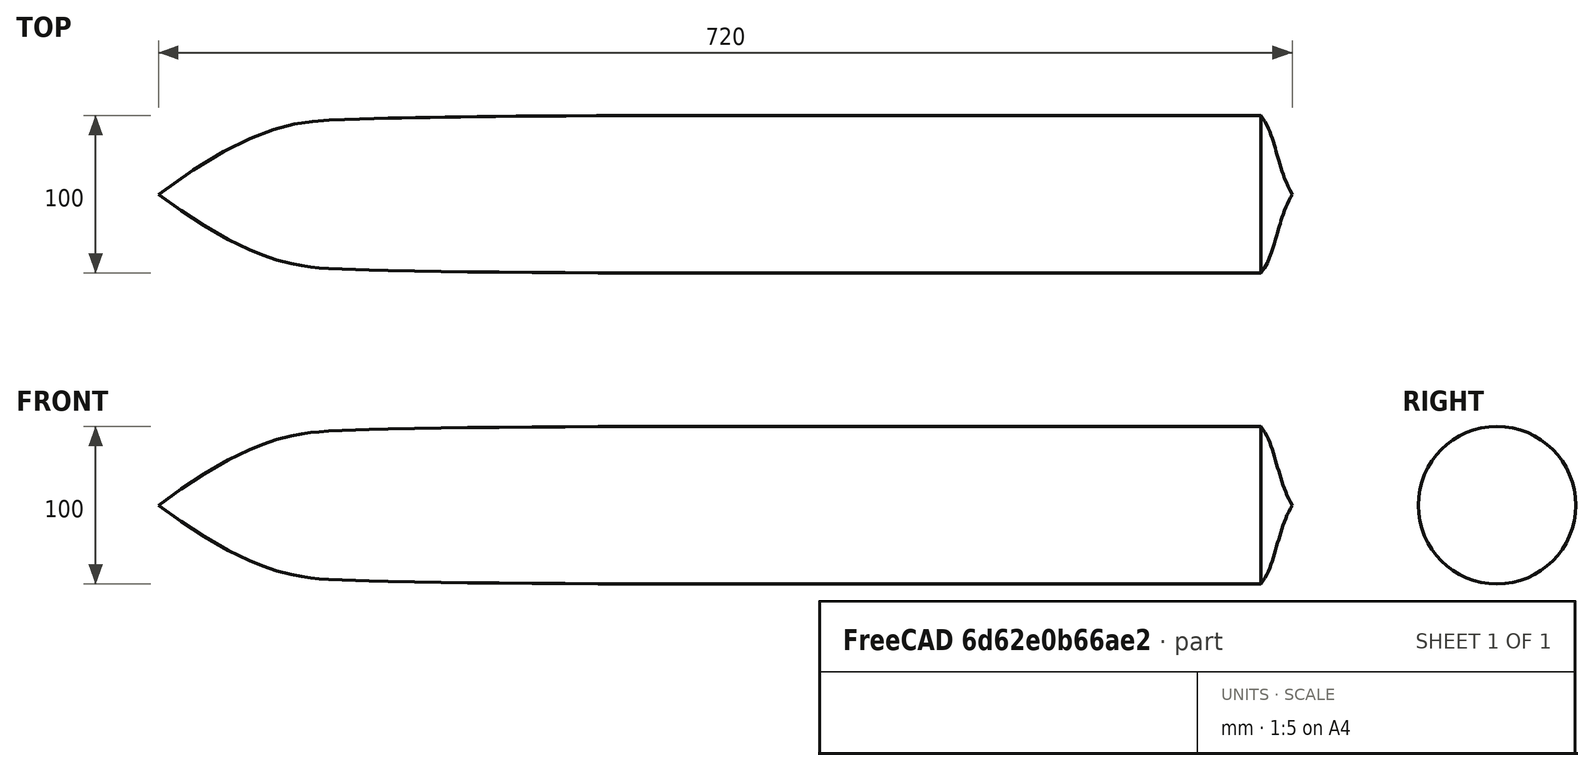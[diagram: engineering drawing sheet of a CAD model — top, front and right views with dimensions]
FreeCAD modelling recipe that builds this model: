
FCSTD DOCUMENT  (FreeCAD 0.19R24267 +99 (Git))
Label: Myring_hull_spreadsheet
License: All rights reserved
LicenseURL: http://en.wikipedia.org/wiki/All_rights_reserved
objects: Sketcher::SketchObject×1, PartDesign::Revolution×1, PartDesign::Body×1, TechDraw::DrawSVGTemplate×1, TechDraw::DrawViewPart×1, TechDraw::DrawViewSection×1, TechDraw::DrawPage×1, Spreadsheet::Sheet×1
note: 4 computed .brp shape members not serialized (recipe doc carries the construction recipe); baked Part::Feature solids carry a one-line shape summary decoded from their .brp

FEATURE [Sketcher::SketchObject] Sketch
  FullyConstrained = true
  MapMode = 5
  Support = -> [XY_Plane]
  expr: .Constraints.tail4_y = <<Parameters>>.tail4_y
  expr: .Constraints.tail2_y = <<Parameters>>.tail2_y
  expr: .Constraints.tail1_y = <<Parameters>>.tail1_y
  expr: .Constraints.nose4_y = <<Parameters>>.nose4_y
  expr: .Constraints.tail3_y = <<Parameters>>.tail3_y
  expr: .Constraints.nose3_y = <<Parameters>>.nose3_y
  expr: .Constraints.nose2_y = <<Parameters>>.nose2_y
  expr: .Constraints.myring_r = <<Parameters>>.myring_r
  expr: .Constraints.tail3_x = .Constraints.myring_c * 0.6
  expr: .Constraints.tail1_x = .Constraints.myring_c * 0.2
  expr: .Constraints.tail4_x = .Constraints.myring_c * 0.8
  expr: .Constraints.nose4_x = .Constraints.myring_a * 4 / 5
  expr: .Constraints.tail2_x = .Constraints.myring_c * 0.4
  expr: .Constraints.nose3_x = .Constraints.myring_a * 3 / 5
  expr: .Constraints.nose2_x = .Constraints.myring_a * 2 / 5
  expr: .Constraints.myring_b = <<Parameters>>.myring_b
  expr: .Constraints.myring_a = <<Parameters>>.myring_a
  expr: .Constraints.nose1_y = <<Parameters>>.nose1_y
  expr: .Constraints.myring_c = <<Parameters>>.myring_c
  expr: Constraints[5] = .Constraints.myring_r
  expr: .Constraints.nose1_x = .Constraints.myring_a * 1 / 5
  sketch-geometry (28):
    g0: LineSegment StartX=200 StartY=50 StartZ=0 EndX=200 EndY=0 EndZ=0
    g1: LineSegment StartX=-200 StartY=50 StartZ=0 EndX=-200 EndY=0 EndZ=0
    g2: LineSegment StartX=-200 StartY=0 StartZ=0 EndX=200 EndY=0 EndZ=0
    g3: LineSegment StartX=-200 StartY=0 StartZ=0 EndX=-500 EndY=0 EndZ=0
    g4: LineSegment StartX=200 StartY=0 StartZ=0 EndX=220 EndY=0 EndZ=0
    g5-g10: Circle x6 (B-spline internal-alignment scaffolding for g11; pole/knot coordinates omitted)
    g11: BSplineCurve PolesCount=6 KnotsCount=4 Degree=3 IsPeriodic=0
    g12-g15: GeomPoint x4 (B-spline internal-alignment scaffolding for g11; pole/knot coordinates omitted)
    g16: LineSegment StartX=-200 StartY=50 StartZ=0 EndX=200 EndY=50 EndZ=0
    g17-g22: Circle x6 (B-spline internal-alignment scaffolding for g23; pole/knot coordinates omitted)
    g23: BSplineCurve PolesCount=6 KnotsCount=4 Degree=3 IsPeriodic=0
    g24-g27: GeomPoint x4 (B-spline internal-alignment scaffolding for g23; pole/knot coordinates omitted)
  constraints (46):
    c: Vertical(g0)
    c: Vertical(g1)
    c: DistanceX(g1,g0) = 400  'myring_b'
    c: Symmetric(g1,g0,g-2)
    c: DistanceY(g0,g0) = 50  'myring_r'
    c: DistanceY(g1,g1) = 50
    c: Coincident(g2,g1)
    c: Coincident(g2,g0)
    c: Coincident(g3,g1)
    c: PointOnObject(g3,g-1)
    c: Horizontal(g3)
    c: Coincident(g4,g0)
    c: PointOnObject(g4,g-1)
    c: DistanceX(g3,g2) = 300  'myring_a'
    c: DistanceX(g2,g4) = 20  'myring_c'
    c: Coincident(g11,g3)
    c: Weight(g5) = 1
    c: Equal(g5, g6-g10) x5
    c: Coincident(g11,g1)
    c: InternalAlignment(g5-g10 -> g11) x6
    c: InternalAlignment(g12-g15 -> g11) x4
    c: DistanceY(g3,g6) = 45.144  'nose1_y'
    c: DistanceY(g3,g7) = 47.8176  'nose2_y'
    c: DistanceY(g3,g8) = 49.1358  'nose3_y'
    c: DistanceY(g3,g9) = 49.7963  'nose4_y'
    c: DistanceX(g3,g6) = 60  'nose1_x'
    c: DistanceX(g3,g7) = 120  'nose2_x'
    c: DistanceX(g3,g8) = 180  'nose3_x'
    c: DistanceX(g3,g9) = 240  'nose4_x'
    c: Coincident(g16,g11)
    c: Horizontal(g16)
    c: Equal(g16,g2)
    c: Coincident(g23,g16)
    c: Weight(g17) = 1
    c: Equal(g17, g18-g22) x5
    c: Coincident(g23,g4)
    c: InternalAlignment(g17-g22 -> g23) x6
    c: InternalAlignment(g24-g27 -> g23) x4
    c: DistanceX(g16,g18) = 4  'tail1_x'
    c: DistanceX(g16,g19) = 8  'tail2_x'
    c: DistanceX(g16,g20) = 12  'tail3_x'
    c: DistanceX(g16,g21) = 16  'tail4_x'
    c: DistanceY(g2,g18) = 45.1695  'tail1_y'
    c: DistanceY(g2,g19) = 33.5085  'tail2_y'
    c: DistanceY(g2,g20) = 19.2628  'tail3_y'
    c: DistanceY(g2,g21) = 6.67802  'tail4_y'
FEATURE [PartDesign::Revolution] Revolution
  Angle = 360
  Axis = (1,0,0)
  Base = (0,0,0)
  Profile = -> Sketch
  ReferenceAxis = -> Sketch [H_Axis]
FEATURE [PartDesign::Body] Body
  Group = -> [Sketch,Revolution]
  Origin = -> Origin
  Tip = -> Revolution
FEATURE [TechDraw::DrawSVGTemplate] Template
  EditableTexts = Designed_by_Name=Designed by Name; Drawing_number=Drawing number; FC-Date=Date; FC-SC=Scale; FC-SH=Sheet; FC-Title=Title; Subtitle=Subtitle; Weight=Weight
  Height = 210
  Orientation = 1
  Width = 297
FEATURE [TechDraw::DrawViewPart] View
  CoarseView = false
  Direction = (0,0,1)
  Focus = 100
  HardHidden = false
  IsoCount = 0
  IsoHidden = false
  IsoVisible = false
  LockPosition = false
  Perspective = false
  Rotation = 0
  Scale = 0.05
  ScaleType = 0
  SeamHidden = false
  SeamVisible = true
  SmoothHidden = false
  SmoothVisible = true
  Source = -> [Body]
  X = 65.7614
  XDirection = (1,0,0)
  Y = 42.7117
FEATURE [TechDraw::DrawViewSection] SectionView  label="Section  - "
  BaseView = -> View
  CoarseView = false
  CutSurfaceDisplay = 2
  Direction = (0,1,0)
  FileGeomPattern = <path>
  FileHatchPattern = <path>
  Focus = 100
  FuseBeforeCut = false
  HardHidden = false
  HatchScale = 1
  IsoCount = 0
  IsoHidden = false
  IsoVisible = false
  LockPosition = false
  NameGeomPattern = Diamond
  Perspective = false
  Rotation = 0
  Scale = 0.1
  ScaleType = 0
  SeamHidden = false
  SeamVisible = true
  SectionDirection = 3
  SectionNormal = (0,1,0)
  SectionOrigin = (0,0,0)
  SmoothHidden = false
  SmoothVisible = true
  Source = -> [Body]
  X = 144.754
  XDirection = (1,0,0)
  Y = 127.102
FEATURE [TechDraw::DrawPage] Page
  KeepUpdated = true
  NextBalloonIndex = 1
  ProjectionType = 0
  Template = -> Template
  Views = -> [View,SectionView]
FEATURE [Spreadsheet::Sheet] Spreadsheet  label="Parameters"
  cells = A1=Hull Nose; B1(myring_a)==300mm; A2=Hull Body; B2(myring_b)==400mm; A3=Hull Tail; B3(myring_c)==20mm; A4=Nose1_y; B4(nose1_y)==45.14402257237171mm; A5=Nose2_y; B5(nose2_y)==47.81762498950185mm; A6=Nose3_y; B6(nose3_y)==49.13578886380858mm; A7=Nose4_y; B7(nose4_y)==49.79630606989253mm; A8=Tail1_y; B8(tail1_y)==45.16950417228136mm; A9=Tail2_y; B9(tail2_y)==33.50851251684409mm; A10=Tail3_y; B10(tail3_y)==19.26276877526612mm; A11=Tail4_y; B11(tail4_y)==6.67801668912545mm; A12=Hull Radius; B12(myring_r)==50mm
note: 2 file-system paths scrubbed to <path> (originals preserved in the JSON sidecar)
